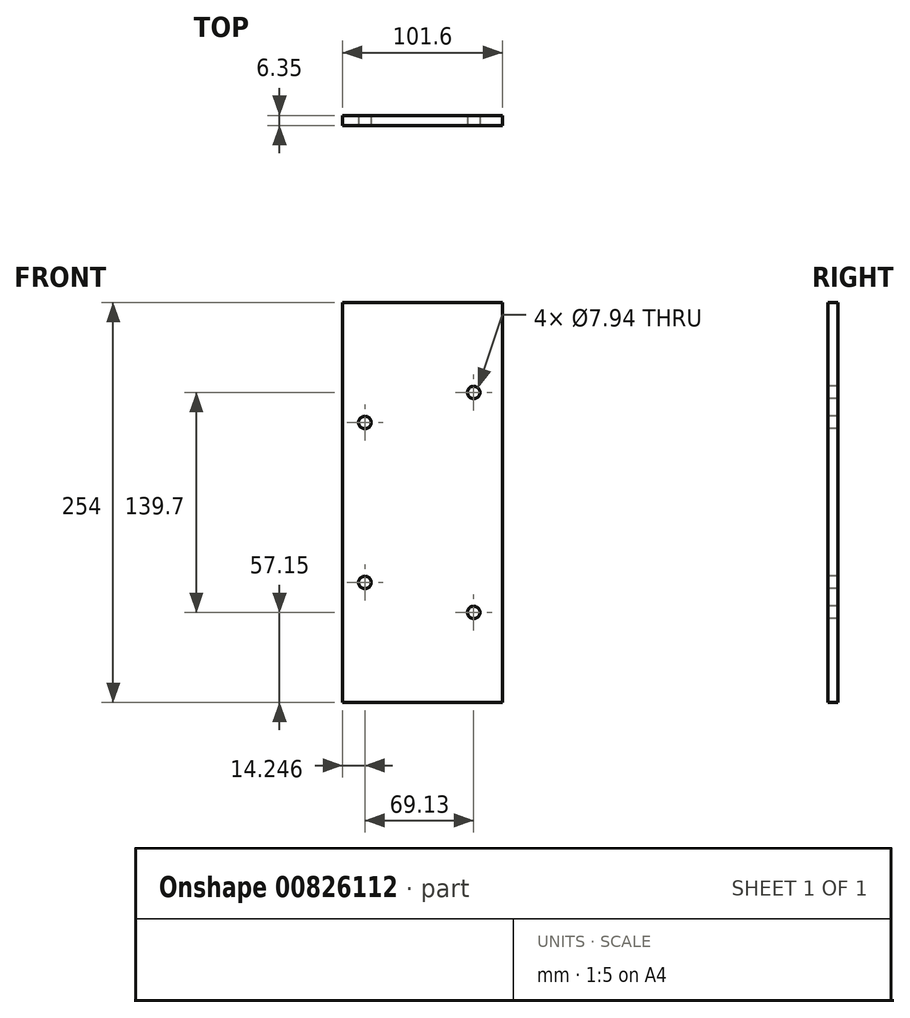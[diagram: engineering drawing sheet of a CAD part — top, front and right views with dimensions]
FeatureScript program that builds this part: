
annotation { "Feature Type Name" : "Feature", "Feature Type Description" : "" }
export const myFeature = defineFeature(function(context is Context, id is Id, definition is map)
    precondition{}
    {
        {
            var Q0;
            Q0=qCreatedBy(makeId("Front.planeOp"),FACE);
            var sketch = newSketch(context, id + "F0", { "sketchPlane" : qUnion([Q0])});
            skLineSegment(sketch, "E0.bottom", {"start": v(0, 0) * mm, "end": v(101.6, 0) * mm});
            skLineSegment(sketch, "E0.top", {"start": v(0, 254) * mm, "end": v(101.6, 254) * mm});
            skLineSegment(sketch, "E0.left", {"start": v(0, 0) * mm, "end": v(0, 254) * mm});
            skLineSegment(sketch, "E0.right", {"start": v(101.6, 0) * mm, "end": v(101.6, 254) * mm});
            skSolve(sketch);
        }
        {
            var Q0;
            Q0=qSketchRegion(id+"F0",true);
            extrude(context, id + "F1", {"entities" : qUnion([Q0]), "depth" : 6.35 * mm, "offsetDistance" : 25.4 * mm});
        }
        {
            var Q0;
            Q0=makeQuery(id+"F1.opExtrude","CAP_FACE",FACE,{"disambiguationData":[OSD([sQuery(id+"F0.wireOp",EDGE,"E0.bottom"),sQuery(id+"F0.wireOp",EDGE,"E0.top"),sQuery(id+"F0.wireOp",EDGE,"E0.left"),sQuery(id+"F0.wireOp",EDGE,"E0.right")])],"isStart":false});
            var sketch = newSketch(context, id + "F2", { "sketchPlane" : qUnion([Q0])});
            skPoint(sketch, "E1", {"position": v(83.38, 57.15) * mm});
            skPoint(sketch, "E2", {"position": v(83.38, 196.85) * mm});
            skSolve(sketch);
        }
        {
            var Q0;
            Q0=sQuery(id+"F2.wireOp",VERTEX,"E1");
            var Q1;
            Q1=sQuery(id+"F2.wireOp",VERTEX,"E2");
            var Q2;
            Q2=makeQuery(id+"F1.opExtrude","SWEPT_BODY",BODY,{"disambiguationData":[OSD([sQuery(id+"F0.wireOp",EDGE,"E0.bottom"),sQuery(id+"F0.wireOp",EDGE,"E0.top"),sQuery(id+"F0.wireOp",EDGE,"E0.left"),sQuery(id+"F0.wireOp",EDGE,"E0.right")])]});
            hole(context, id + "F3", {"style" : HoleStyle.SIMPLE, "endStyle" : HoleEndStyle.THROUGH, "holeDiameter" : 7.94 * mm, "majorDiameter" : 6.35 * mm, "isTappedThrough" : true, "tappedDepth" : 12.7 * mm, "tapClearance" : 3, "locations" : qUnion([Q0, Q1]), "scope" : qUnion([Q2])});
        }
        {
            var Q0;
            Q0=makeQuery(id+"F1.opExtrude","CAP_FACE",FACE,{"disambiguationData":[OSD([sQuery(id+"F0.wireOp",EDGE,"E0.bottom"),sQuery(id+"F0.wireOp",EDGE,"E0.top"),sQuery(id+"F0.wireOp",EDGE,"E0.left"),sQuery(id+"F0.wireOp",EDGE,"E0.right")])],"isStart":false});
            var sketch = newSketch(context, id + "F4", { "sketchPlane" : qUnion([Q0])});
            skPoint(sketch, "E3", {"position": v(14.25, 76.2) * mm});
            skPoint(sketch, "E4", {"position": v(14.25, 177.8) * mm});
            skSolve(sketch);
        }
        {
            var Q0;
            Q0=sQuery(id+"F4.wireOp",VERTEX,"E3");
            var Q1;
            Q1=sQuery(id+"F4.wireOp",VERTEX,"E4");
            var Q2;
            Q2=makeQuery(id+"F1.opExtrude","SWEPT_BODY",BODY,{"disambiguationData":[OSD([sQuery(id+"F0.wireOp",EDGE,"E0.bottom"),sQuery(id+"F0.wireOp",EDGE,"E0.top"),sQuery(id+"F0.wireOp",EDGE,"E0.left"),sQuery(id+"F0.wireOp",EDGE,"E0.right")])]});
            hole(context, id + "F5", {"style" : HoleStyle.SIMPLE, "endStyle" : HoleEndStyle.THROUGH, "holeDiameter" : 7.94 * mm, "majorDiameter" : 6.35 * mm, "isTappedThrough" : true, "tappedDepth" : 12.7 * mm, "tapClearance" : 3, "locations" : qUnion([Q0, Q1]), "scope" : qUnion([Q2])});
        }
    });
